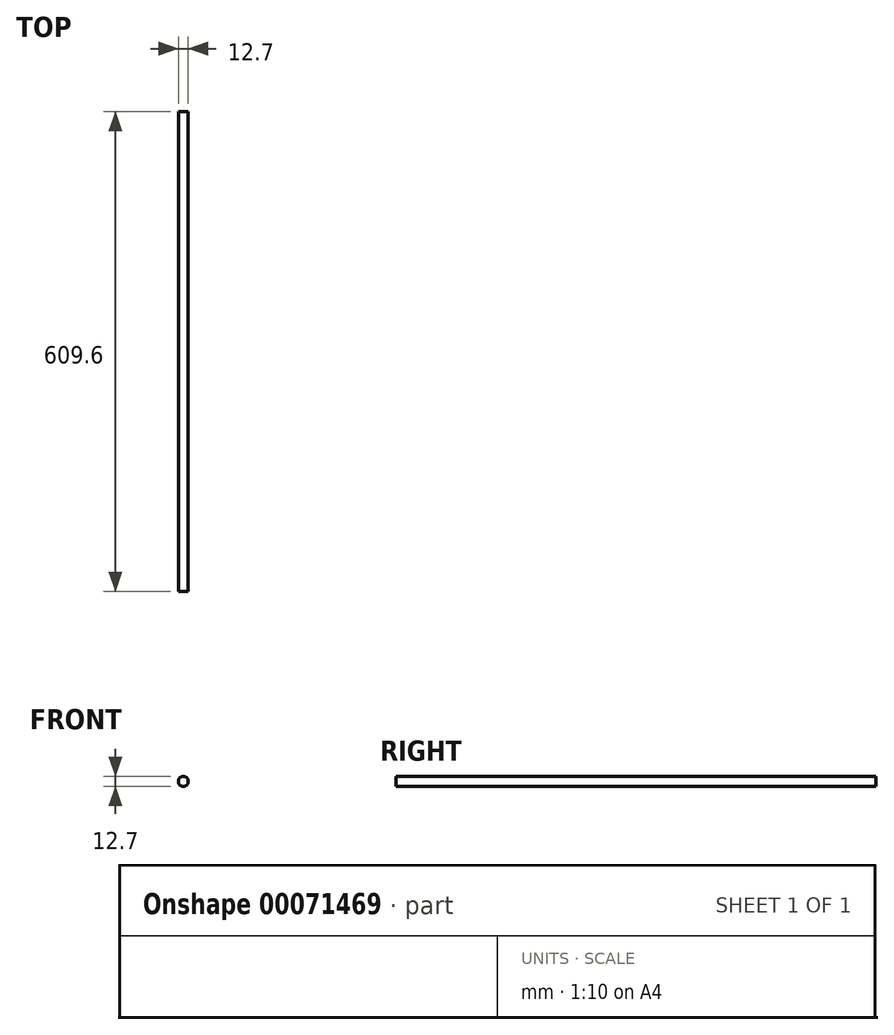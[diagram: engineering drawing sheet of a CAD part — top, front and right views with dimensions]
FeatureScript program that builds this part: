
annotation { "Feature Type Name" : "Feature", "Feature Type Description" : "" }
export const myFeature = defineFeature(function(context is Context, id is Id, definition is map)
    precondition{}
    {
        {
            var Q0;
            Q0=qCreatedBy(makeId("Front.planeOp"),FACE);
            var sketch = newSketch(context, id + "F0", { "sketchPlane" : qUnion([Q0])});
            skCircle(sketch, "E0", {"center": v(0, 0) * mm, "radius": 6.35 * mm});
            skSolve(sketch);
        }
        {
            var Q0;
            Q0=makeQuery(id+"F0.imprint","IMPRINT",FACE,{"disambiguationData":[TD([[makeQuery(id+"F0.imprint","IMPRINT",EDGE,{"derivedFrom":sQuery(id+"F0.wireOp",EDGE,"E0")}),1.0]])]});
            extrude(context, id + "F1", {"entities" : qUnion([Q0]), "depth" : 609.6 * mm});
        }
    });
